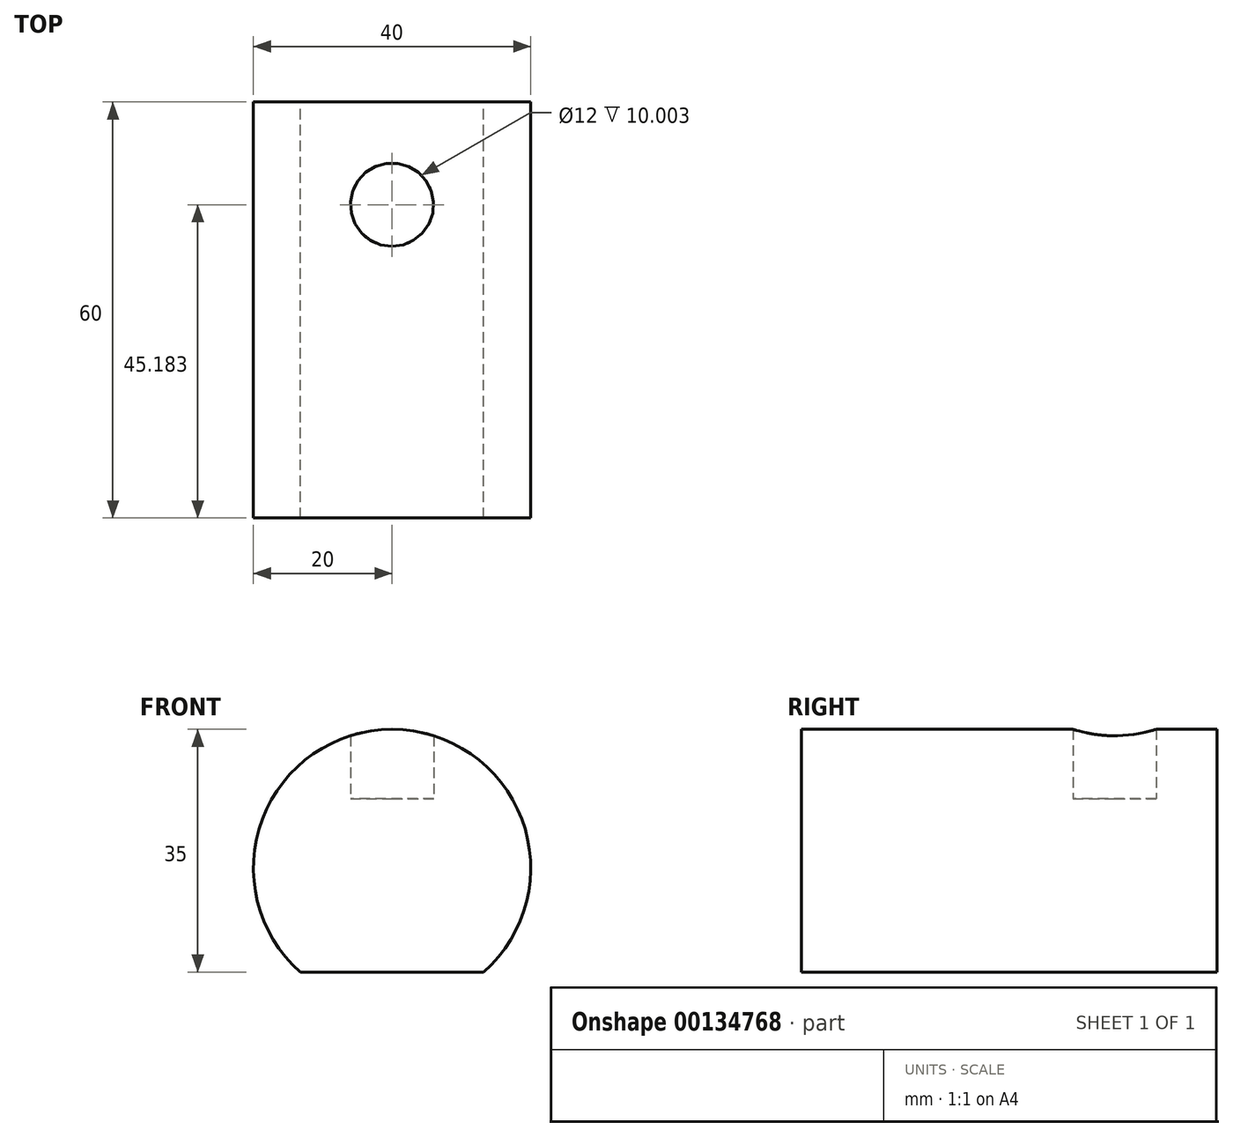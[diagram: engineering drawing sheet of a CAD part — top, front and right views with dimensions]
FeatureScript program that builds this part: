
annotation { "Feature Type Name" : "Feature", "Feature Type Description" : "" }
export const myFeature = defineFeature(function(context is Context, id is Id, definition is map)
    precondition{}
    {
        {
            var Q0;
            Q0=qCreatedBy(makeId("Front.planeOp"),FACE);
            var sketch = newSketch(context, id + "F0", { "sketchPlane" : qUnion([Q0])});
            skCircle(sketch, "E0", {"center": v(0, 0) * mm, "radius": 20 * mm});
            skSolve(sketch);
        }
        {
            var Q0;
            Q0 = qSketchRegion(id + "F0", true);
            extrude(context, id + "F1", {"entities" : qUnion([Q0]), "depth" : 60 * mm});
        }
        {
            var Q0;
            Q0=qCreatedBy(makeId("Top.planeOp"),FACE);
            cPlane(context, id + "F2", {"entities" : qUnion([Q0]), "cplaneType" : CPlaneType.OFFSET, "offset" : 10 * mm, "width" : 150 * mm, "height" : 150 * mm});
        }
        {
            var Q0;
            Q0=qCreatedBy(id+"F2.planeOp",FACE);
            var sketch = newSketch(context, id + "F3", { "sketchPlane" : qUnion([Q0])});
            skCircle(sketch, "E1", {"center": v(0, -14.82) * mm, "radius": 6 * mm});
            skSolve(sketch);
        }
        {
            var Q0;
            Q0 = qSketchRegion(id + "F3", true);
            extrude(context, id + "F4", {"entities" : qUnion([Q0]), "operationType" : NewBodyOperationType.REMOVE, "depth" : 23.6 * mm});
        }
        {
            var Q0;
            Q0=makeQuery(id+"F1.opExtrude","CAP_FACE",FACE,{"disambiguationData":[OSD([sQuery(id+"F0.wireOp",EDGE,"E0")])],"isStart":false});
            var sketch = newSketch(context, id + "F5", { "sketchPlane" : qUnion([Q0])});
            skLineSegment(sketch, "E2.bottom", {"start": v(-32.1, -32.17) * mm, "end": v(47.25, -32.17) * mm});
            skLineSegment(sketch, "E2.top", {"start": v(-32.1, -15) * mm, "end": v(47.25, -15) * mm});
            skLineSegment(sketch, "E2.left", {"start": v(-32.1, -32.17) * mm, "end": v(-32.1, -15) * mm});
            skLineSegment(sketch, "E2.right", {"start": v(47.25, -32.17) * mm, "end": v(47.25, -15) * mm});
            skSolve(sketch);
        }
        {
            var Q0;
            Q0 = qSketchRegion(id + "F5", true);
            extrude(context, id + "F6", {"entities" : qUnion([Q0]), "operationType" : NewBodyOperationType.REMOVE, "oppositeDirection" : true, "depth" : 121.24 * mm});
        }
    });
